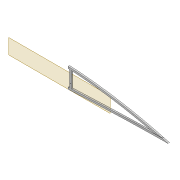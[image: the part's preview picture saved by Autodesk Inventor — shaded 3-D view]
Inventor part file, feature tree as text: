
AUTODESK INVENTOR PART (.ipt)
format: ipt  version: 2022 (Build 260153000, 153)  size: 425,984 bytes
history: native  units: mm
features: extrude x9, sketch x7, projected_geometry x6, fillet x2, shell x1, plane x1
ambient origin geometry x8: Origin, YZ Plane, XZ Plane, XY Plane, X Axis, Y Axis, Z Axis, Center Point
bodies: Solid1 (feature_tree)
feature tree (26):
  extrude  "Extrusion1"  Depth=5.0mm
  shell  "Shell1"  Thickness=2.0mm
  extrude  "Extrusion8"  Depth=5.9mm
  extrude  "Extrusion3"  Depth=10.0mm TaperAngle=0.0deg
  extrude  "Extrusion4"  Depth=2.0mm
  fillet  "Fillet1"  Radius=5.0mm
  sketch  "Sketch10"  dims[d22=4.0mm d23=0.0mm d31=2.0mm d32=5.0mm]
  extrude  "Extrusion5"  Depth=2.5mm
  plane  "Work Plane2"
  extrude  "Extrusion9"  Depth=1.6mm
  extrude  "Extrusion10"  Depth=80.0mm
  fillet  "Fillet2"  Radius=6.0mm
  extrude  "Extrusion11"  Depth=4.0mm TaperAngle=0.0deg
  extrude  "Extrusion12"  Depth=3.0mm
  sketch  "Sketch3"  dims[d0=4.0mm d1=0.0mm d2=5.0mm d7=2.0mm]
  sketch  "Sketch8"  dims[d8=2.0mm d9=5.9mm]
  sketch  "Sketch9"  dims[d13=10.0mm d14=0.0mm d16=10.0mm d17=0.0mm]
  projected_geometry  "Projected Loop4"
  projected_geometry  "Projected Loop10"
  sketch  "Sketch24"  dims[d34=1.6mm d35=2.5mm]
  projected_geometry  "Projected Loop11"
  projected_geometry  "Projected Loop12"
  projected_geometry  "Projected Loop13"
  sketch  "Sketch26"  dims[d37=5.0mm d38=1.6mm]
  projected_geometry  "Projected Loop14"
  sketch  "Sketch27"  dims[d40=2.5mm d62=80.0mm d63=6.0mm d64=4.0mm d65=0.0mm d66=3.0mm d67=12.0mm d68=5.0mm d69=25.0mm d70=12.0mm d71=3.05mm d72=4.0mm d73=0.0mm d74=10.0mm d75=0.0mm d76=2.0mm d77=100.0mm d78=20.0mm d79=0.5mm d80=10.0mm d81=0.0mm d82=10.0mm d83=0.0mm]
